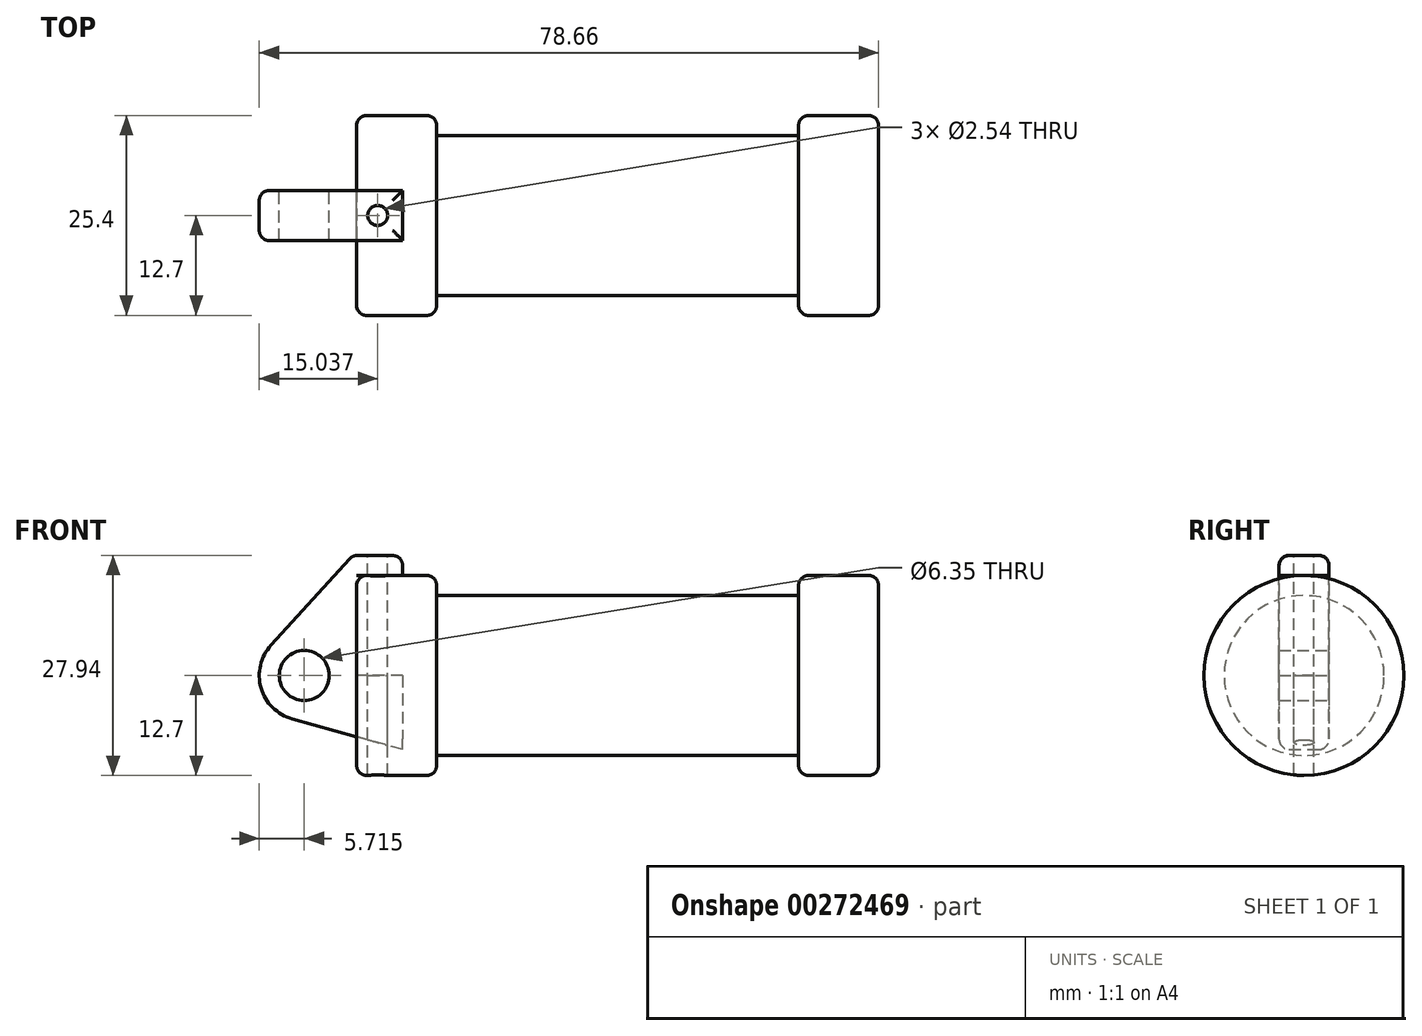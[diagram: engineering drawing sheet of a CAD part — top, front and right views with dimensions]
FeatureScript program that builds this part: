
annotation { "Feature Type Name" : "Feature", "Feature Type Description" : "" }
export const myFeature = defineFeature(function(context is Context, id is Id, definition is map)
    precondition{}
    {
        {
            var Q0;
            Q0=qCreatedBy(makeId("Front.planeOp"),FACE);
            var sketch = newSketch(context, id + "F0", { "sketchPlane" : qUnion([Q0])});
            skLineSegment(sketch, "E0", {"start": v(0, 0) * mm, "end": v(0, 12.7) * mm});
            skLineSegment(sketch, "E1", {"start": v(0, 12.7) * mm, "end": v(10.16, 12.7) * mm});
            skLineSegment(sketch, "E2", {"start": v(10.16, 12.7) * mm, "end": v(10.16, 10.16) * mm});
            skLineSegment(sketch, "E3", {"start": v(10.16, 10.16) * mm, "end": v(56.13, 10.16) * mm});
            skLineSegment(sketch, "E4", {"start": v(56.13, 10.16) * mm, "end": v(56.13, 12.7) * mm});
            skLineSegment(sketch, "E5", {"start": v(56.13, 12.7) * mm, "end": v(66.3, 12.7) * mm});
            skLineSegment(sketch, "E6", {"start": v(66.3, 12.7) * mm, "end": v(66.3, 0) * mm});
            skLineSegment(sketch, "E7", {"start": v(66.3, 0) * mm, "end": v(0, 0) * mm});
            skLineSegment(sketch, "E8", {"start": v(5.84, 15.24) * mm, "end": v(-0.5, 15.24) * mm});
            skLineSegment(sketch, "E9", {"start": v(-0.5, 15.24) * mm, "end": v(-10.88, 3.85) * mm});
            skLineSegment(sketch, "E10", {"start": v(0, 0) * mm, "end": v(-6.65, 0) * mm});
            skCircle(sketch, "E11", {"center": v(-6.65, 0) * mm, "radius": 5.72 * mm});
            skCircle(sketch, "E12", {"center": v(-6.65, 0) * mm, "radius": 3.18 * mm});
            skLineSegment(sketch, "E13", {"start": v(5.84, 15.24) * mm, "end": v(5.84, -9.4) * mm});
            skLineSegment(sketch, "E14", {"start": v(5.84, -9.4) * mm, "end": v(-8.18, -5.5) * mm});
            skSolve(sketch);
        }
        {
            var Q0;
            {var subQ0=sQuery(id+"F0.wireOp",EDGE,"E2");Q0=makeQuery(id+"F0.imprint","IMPRINT",FACE,{"disambiguationData":[TD([[makeQuery(id+"F0.imprint","IMPRINT",EDGE,{"derivedFrom":subQ0}),-1.0]])]});}
            var Q1;
            {var subQ0=sQuery(id+"F0.wireOp",EDGE,"E0");Q1=makeQuery(id+"F0.imprint","IMPRINT",FACE,{"disambiguationData":[TD([[makeQuery(id+"F0.imprint","IMPRINT",EDGE,{"derivedFrom":subQ0}),-1.0]])]});}
            var Q2;
            Q2=sQuery(id+"F0.wireOp",EDGE,"E7");
            revolve(context, id + "F1", {"entities" : qUnion([Q0, Q1]), "axis" : qUnion([Q2]), "revolveType" : RevolveType.FULL});
        }
        {
            var Q0;
            {var subQ3=sQuery(id+"F0.wireOp",EDGE,"E0");Q0=makeQuery(id+"F0.imprint","IMPRINT",FACE,{"disambiguationData":[TD([[makeQuery(id+"F0.imprint","IMPRINT",EDGE,{"derivedFrom":subQ3}),1.0]])]});}
            var Q1;
            {var subQ4=sQuery(id+"F0.wireOp",EDGE,"E12");Q1=makeQuery(id+"F0.imprint","IMPRINT",FACE,{"disambiguationData":[TD([[makeQuery(id+"F0.imprint","IMPRINT",EDGE,{"derivedFrom":subQ4}),-1.0]])]});}
            var Q2;
            {var subQ0=sQuery(id+"F0.wireOp",EDGE,"E14");Q2=makeQuery(id+"F0.imprint","IMPRINT",FACE,{"disambiguationData":[TD([[makeQuery(id+"F0.imprint","IMPRINT",EDGE,{"derivedFrom":subQ0}),-1.0]])]});}
            extrude(context, id + "F2", {"entities" : qUnion([Q0, Q1, Q2]), "endBound" : BoundingType.SYMMETRIC, "depth" : 6.35 * mm});
        }
        {
            var Q0;
            Q0=makeQuery(id+"F1.opRevolve","SWEPT_FACE",FACE,{"disambiguationData":[OSD([sQuery(id+"F0.wireOp",EDGE,"E6")])]});
            var sketch = newSketch(context, id + "F3", { "sketchPlane" : qUnion([Q0])});
            skCircle(sketch, "E15", {"center": v(0, 0) * mm, "radius": 1.52 * mm});
            skCircle(sketch, "E16", {"center": v(0, 0) * mm, "radius": 5.08 * mm});
            skLineSegment(sketch, "E17", {"start": v(-5.08, 0) * mm, "end": v(-5.08, 15.24) * mm});
            skLineSegment(sketch, "E18", {"start": v(5.08, 0) * mm, "end": v(5.08, 15.24) * mm});
            skLineSegment(sketch, "E19", {"start": v(-5.08, 15.24) * mm, "end": v(5.08, 15.24) * mm});
            skSolve(sketch);
        }
        {
            var Q0;
            Q0=makeQuery(id+"F2.opExtrude","SWEPT_FACE",FACE,{"disambiguationData":[OSD([sQuery(id+"F0.wireOp",EDGE,"E8")])]});
            var sketch = newSketch(context, id + "F4", { "sketchPlane" : qUnion([Q0])});
            skPoint(sketch, "E20", {"position": v(2.67, 0) * mm});
            skPoint(sketch, "E20.positionSnap0", {"position": v(5.84, 0) * mm});
            skPoint(sketch, "E20.positionSnap1", {"position": v(2.67, 3.18) * mm});
            skSolve(sketch);
        }
        {
            var Q0;
            Q0=sQuery(id+"F4.wireOp",VERTEX,"E20");
            var Q1;
            Q1=makeQuery(id+"F1.opRevolve","SWEPT_BODY",BODY,{"disambiguationData":[OSD([sQuery(id+"F0.wireOp",EDGE,"E0"),sQuery(id+"F0.wireOp",EDGE,"E1"),sQuery(id+"F0.wireOp",EDGE,"E2"),sQuery(id+"F0.wireOp",EDGE,"E3"),sQuery(id+"F0.wireOp",EDGE,"E4"),sQuery(id+"F0.wireOp",EDGE,"E5"),sQuery(id+"F0.wireOp",EDGE,"E6"),sQuery(id+"F0.wireOp",EDGE,"E7")])]});
            var Q2;
            Q2=makeQuery(id+"F2.opExtrude","SWEPT_BODY",BODY,{"disambiguationData":[OSD([sQuery(id+"F0.wireOp",EDGE,"E0"),sQuery(id+"F0.wireOp",EDGE,"E1"),sQuery(id+"F0.wireOp",EDGE,"E7"),sQuery(id+"F0.wireOp",EDGE,"E8"),sQuery(id+"F0.wireOp",EDGE,"E9"),sQuery(id+"F0.wireOp",EDGE,"E11"),sQuery(id+"F0.wireOp",EDGE,"E12"),sQuery(id+"F0.wireOp",EDGE,"E13"),sQuery(id+"F0.wireOp",EDGE,"E14")])]});
            hole(context, id + "F5", {"style" : HoleStyle.SIMPLE, "endStyle" : HoleEndStyle.THROUGH, "holeDiameter" : 2.54 * mm, "tappedDepth" : 12.7 * mm, "tapClearance" : 3, "locations" : qUnion([Q0]), "scope" : qUnion([Q1, Q2])});
        }
        {
            var Q0;
            Q0=makeQuery(id+"F2.opExtrude","CAP_EDGE",EDGE,{"disambiguationData":[OSD([sQuery(id+"F0.wireOp",EDGE,"E8")])],"isStart":false});
            var Q1;
            Q1=makeQuery(id+"F1.opRevolve","SWEPT_EDGE",EDGE,{"disambiguationData":[OSD([sQuery(id+"F0.wireOp",EDGE,"E0"),sQuery(id+"F0.wireOp",EDGE,"E1")])]});
            var Q2;
            Q2=makeQuery(id+"F1.opRevolve","SWEPT_EDGE",EDGE,{"disambiguationData":[OSD([sQuery(id+"F0.wireOp",EDGE,"E1"),sQuery(id+"F0.wireOp",EDGE,"E2")])]});
            var Q3;
            Q3=makeQuery(id+"F2.opExtrude","CAP_EDGE",EDGE,{"disambiguationData":[OSD([sQuery(id+"F0.wireOp",EDGE,"E9")])],"isStart":false});
            var Q4;
            Q4=makeQuery(id+"F2.opExtrude","CAP_EDGE",EDGE,{"disambiguationData":[OSD([sQuery(id+"F0.wireOp",EDGE,"E11")])],"isStart":false});
            var Q5;
            Q5=makeQuery(id+"F2.opExtrude","CAP_EDGE",EDGE,{"disambiguationData":[OSD([sQuery(id+"F0.wireOp",EDGE,"E14")])],"isStart":false});
            var Q6;
            Q6=makeQuery(id+"F2.opExtrude","CAP_EDGE",EDGE,{"disambiguationData":[OSD([sQuery(id+"F0.wireOp",EDGE,"E9")])],"isStart":true});
            var Q7;
            Q7=makeQuery(id+"F2.opExtrude","CAP_EDGE",EDGE,{"disambiguationData":[OSD([sQuery(id+"F0.wireOp",EDGE,"E11")])],"isStart":true});
            var Q8;
            Q8=makeQuery(id+"F2.opExtrude","CAP_EDGE",EDGE,{"disambiguationData":[OSD([sQuery(id+"F0.wireOp",EDGE,"E14")])],"isStart":true});
            var Q9;
            Q9=makeQuery(id+"F1.opRevolve","SWEPT_EDGE",EDGE,{"disambiguationData":[OSD([sQuery(id+"F0.wireOp",EDGE,"E5"),sQuery(id+"F0.wireOp",EDGE,"E6")])]});
            var Q10;
            {var subQ0=sQuery(id+"F0.wireOp",EDGE,"E5");Q10=makeQuery(id+"FLUyNNVB3hGT3aS_2.boolean.opBoolean","MERGE",FACE,{"derivedFrom":[makeQuery(id+"F1.opRevolve","SWEPT_FACE",FACE,{"disambiguationData":[OSD([subQ0])]}),makeQuery(id+"FLUyNNVB3hGT3aS_2.opExtrude","SWEPT_FACE",FACE,{"disambiguationData":[OSD([subQ0,sQuery(id+"F0.wireOp",EDGE,"E6")])]})]});}
            var Q11;
            Q11=makeQuery(id+"FLUyNNVB3hGT3aS_2.opExtrude","CAP_EDGE",EDGE,{"disambiguationData":[OSD([sQuery(id+"F3.wireOp",EDGE,"NooJ4l9M-jo5R-6vQp-QKmX-g00ErGKbM202")])],"isStart":false});
            var Q12;
            Q12=makeQuery(id+"FLUyNNVB3hGT3aS_2.boolean.opBoolean","INTERSECT",EDGE,{"derivedFrom":[makeQuery(id+"F1.opRevolve","SWEPT_FACE",FACE,{"disambiguationData":[OSD([sQuery(id+"F0.wireOp",EDGE,"E6")])]}),makeQuery(id+"FLUyNNVB3hGT3aS_2.opExtrude","SWEPT_FACE",FACE,{"disambiguationData":[OSD([sQuery(id+"F3.wireOp",EDGE,"NooJ4l9M-jo5R-6vQp-QKmX-g00ErGKbM202")])]})]});
            var Q13;
            Q13=makeQuery(id+"FLUyNNVB3hGT3aS_2.opExtrude","CAP_EDGE",EDGE,{"disambiguationData":[OSD([sQuery(id+"F3.wireOp",EDGE,"E16")])],"isStart":false});
            var Q14;
            Q14=makeQuery(id+"FLUyNNVB3hGT3aS_2.opExtrude","CAP_EDGE",EDGE,{"disambiguationData":[OSD([sQuery(id+"F3.wireOp",EDGE,"cpAn4Bda-8Uhb-qK88-aIPa-XG85TbJLoU7a")])],"isStart":false});
            var Q15;
            Q15=makeQuery(id+"FLUyNNVB3hGT3aS_2.boolean.opBoolean","INTERSECT",EDGE,{"derivedFrom":[makeQuery(id+"F1.opRevolve","SWEPT_FACE",FACE,{"disambiguationData":[OSD([sQuery(id+"F0.wireOp",EDGE,"E6")])]}),makeQuery(id+"FLUyNNVB3hGT3aS_2.opExtrude","SWEPT_FACE",FACE,{"disambiguationData":[OSD([sQuery(id+"F3.wireOp",EDGE,"E16")])]})]});
            var Q16;
            Q16=makeQuery(id+"FLUyNNVB3hGT3aS_2.opExtrude","CAP_EDGE",EDGE,{"disambiguationData":[OSD([sQuery(id+"F3.wireOp",EDGE,"E15")])],"isStart":false});
            var Q17;
            Q17=makeQuery(id+"F5.hole-0.boolean.opBoolean","COPY",EDGE,{"derivedFrom":makeQuery(id+"F5.hole-0.opRevolve","SWEPT_EDGE",EDGE,{"disambiguationData":[OSD([sQuery(id+"F5.hole-0.sketch.wireOp",EDGE,"core_line_2"),sQuery(id+"F5.hole-0.sketch.wireOp",EDGE,"core_line_3")])]})});
            var Q18;
            Q18=makeQuery(id+"F2.opExtrude","SWEPT_EDGE",EDGE,{"disambiguationData":[OSD([sQuery(id+"F0.wireOp",EDGE,"E8"),sQuery(id+"F0.wireOp",EDGE,"E13")])]});
            var Q19;
            Q19=makeQuery(id+"F2.opExtrude","CAP_EDGE",EDGE,{"disambiguationData":[OSD([sQuery(id+"F0.wireOp",EDGE,"E8")])],"isStart":true});
            var Q20;
            Q20=makeQuery(id+"F2.opExtrude","SWEPT_EDGE",EDGE,{"disambiguationData":[OSD([sQuery(id+"F0.wireOp",EDGE,"E8"),sQuery(id+"F0.wireOp",EDGE,"E9")])]});
            fillet(context, id + "F6", {"entities" : qUnion([Q0, Q1, Q2, Q3, Q4, Q5, Q6, Q7, Q8, Q9, Q10, Q11, Q12, Q13, Q14, Q15, Q16, Q17, Q18, Q19, Q20]), "radius" : 1.27 * mm, "tangentPropagation" : true, "allowEdgeOverflow" : false});
        }
    });
